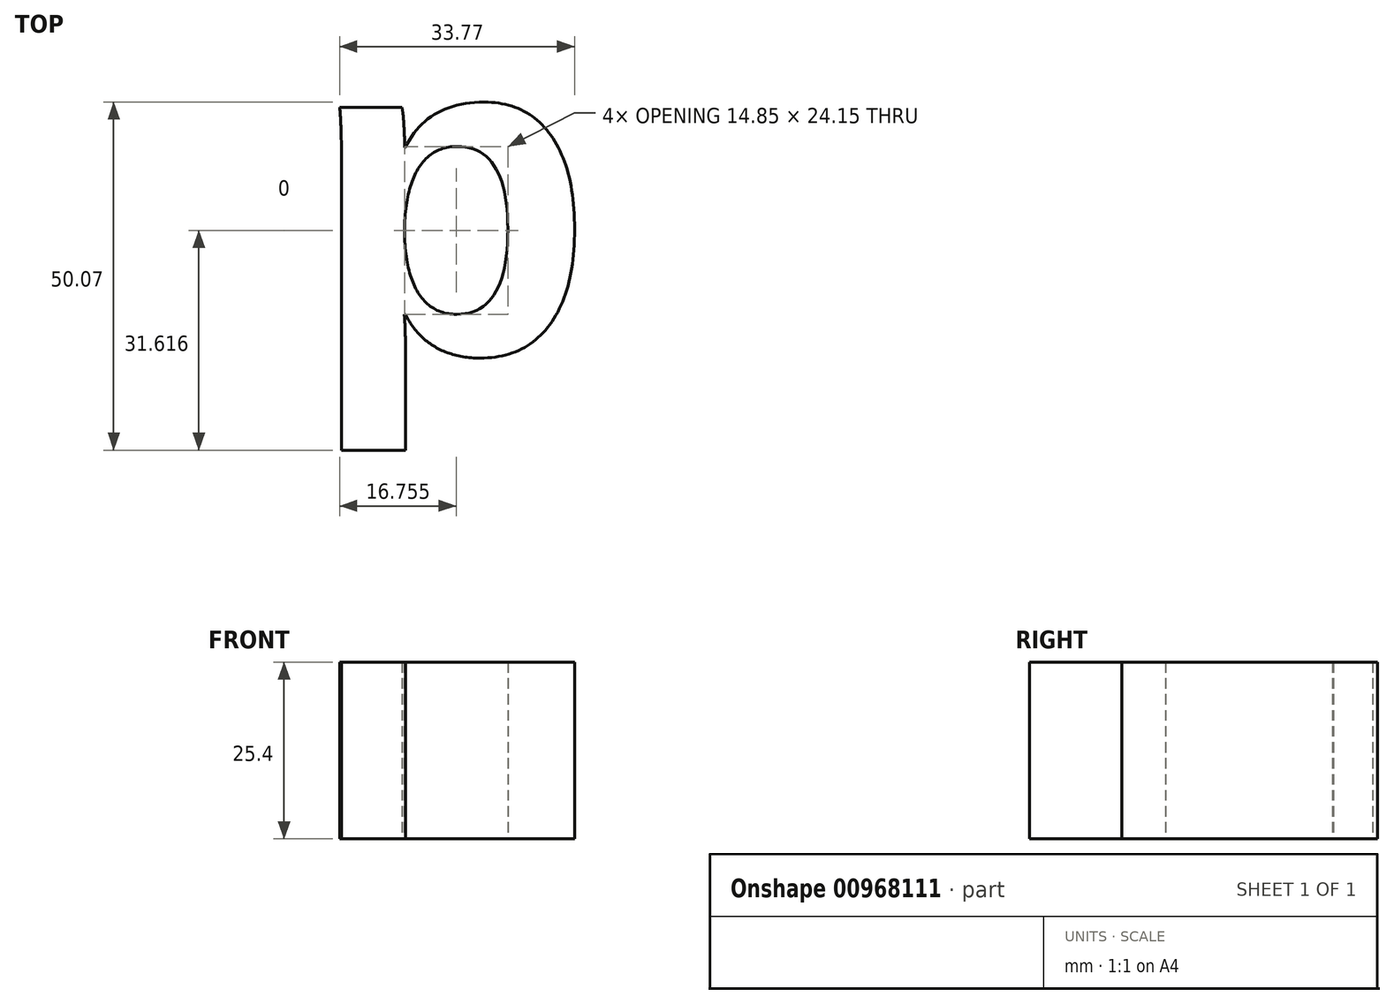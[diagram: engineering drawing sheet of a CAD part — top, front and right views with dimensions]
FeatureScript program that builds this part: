
annotation { "Feature Type Name" : "Feature", "Feature Type Description" : "" }
export const myFeature = defineFeature(function(context is Context, id is Id, definition is map)
    precondition{}
    {
        {
            var Q0;
            Q0=qCreatedBy(makeId("Top.planeOp"),FACE);
            var sketch = newSketch(context, id + "F0", { "sketchPlane" : qUnion([Q0])});
            skText(sketch, "E0", { "text": "Happy 21st", "fontName": "Arimo-Bold.ttf"});
            const initialGuessF0  = {"E0": [-0.1605, -0.01968, 1, 0, 0.04825]};
            skSetInitialGuess(sketch, initialGuessF0);
            skSolve(sketch);
        }
        {
            var Q0;
            Q0=makeQuery(id+"F0.imprint","IMPRINT",FACE,{"disambiguationData":[TD([[makeQuery(id+"F0.imprint","IMPRINT",EDGE,{"derivedFrom":sQuery(id+"F0.wireOp",EDGE,"E0.sketch_text.stroke-50")}),-1.0]])]});
            extrude(context, id + "F1", {"entities" : qUnion([Q0]), "depth" : 25.4 * mm, "offsetDistance" : 25.4 * mm});
        }
    });
